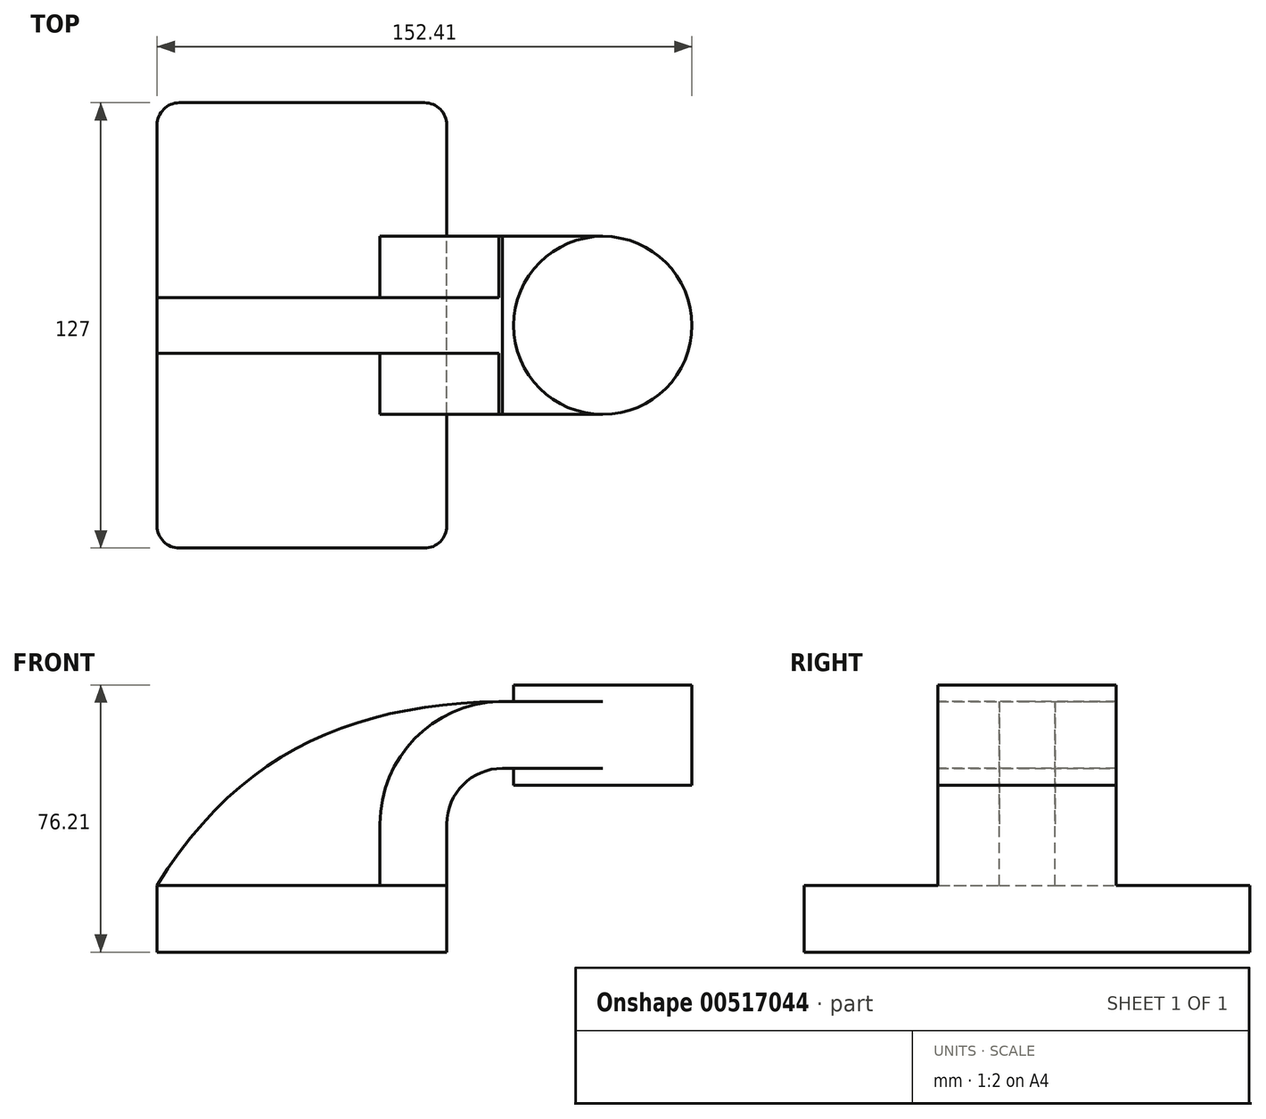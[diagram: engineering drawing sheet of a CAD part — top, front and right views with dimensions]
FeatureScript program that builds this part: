
annotation { "Feature Type Name" : "Feature", "Feature Type Description" : "" }
export const myFeature = defineFeature(function(context is Context, id is Id, definition is map)
    precondition{}
    {
        {
            var Q0;
            Q0=qCreatedBy(makeId("Front.planeOp"),FACE);
            var sketch = newSketch(context, id + "F0", { "sketchPlane" : qUnion([Q0])});
            skLineSegment(sketch, "E0.bottom", {"start": v(-41.28, 9.52) * mm, "end": v(41.27, 9.53) * mm});
            skLineSegment(sketch, "E0.top", {"start": v(-41.28, -9.53) * mm, "end": v(41.28, -9.53) * mm});
            skLineSegment(sketch, "E0.left", {"start": v(-41.28, 9.52) * mm, "end": v(-41.27, -9.53) * mm});
            skLineSegment(sketch, "E0.right", {"start": v(41.28, 9.53) * mm, "end": v(41.28, -9.52) * mm});
            skPoint(sketch, "E0.middle", {"position": v(0, 0) * mm});
            skLineSegment(sketch, "E1.bottom", {"start": v(60.32, 66.68) * mm, "end": v(111.12, 66.68) * mm});
            skLineSegment(sketch, "E1.top", {"start": v(60.32, 38.1) * mm, "end": v(111.12, 38.1) * mm});
            skLineSegment(sketch, "E1.left", {"start": v(60.32, 66.68) * mm, "end": v(60.32, 38.1) * mm});
            skLineSegment(sketch, "E1.right", {"start": v(111.12, 66.68) * mm, "end": v(111.12, 38.1) * mm});
            skPoint(sketch, "E1.middle", {"position": v(85.72, 52.39) * mm});
            skLineSegment(sketch, "E2", {"start": v(41.27, 9.53) * mm, "end": v(41.27, 27) * mm});
            skArc(sketch, "E3", {"start": v(41.27, 27) * mm, "mid": v(45.92, 38.23) * mm, "end": v(57.15, 42.88) * mm});
            skLineSegment(sketch, "E4", {"start": v(57.15, 42.88) * mm, "end": v(85.72, 42.88) * mm});
            skLineSegment(sketch, "E5.0", {"start": v(57.15, 61.93) * mm, "end": v(85.72, 61.93) * mm});
            skArc(sketch, "E5.1", {"start": v(22.23, 27) * mm, "mid": v(32.45, 51.7) * mm, "end": v(57.15, 61.93) * mm});
            skLineSegment(sketch, "E5.2", {"start": v(22.22, 9.53) * mm, "end": v(22.22, 27) * mm});
            skFitSpline(sketch, "E6", {"points": [v(-41.28, 9.53) * mm, v(57.15, 61.93) * mm], "startDerivative": vector(69.81, 113.57) * mm, "endDerivative": vector(128.26, 1.5) * mm});
            skLineSegment(sketch, "E7", {"start": v(85.72, 38.1) * mm, "end": v(85.72, 66.68) * mm});
            skSolve(sketch);
        }
        {
            var Q0;
            Q0=makeQuery(id+"F0.imprint","IMPRINT",FACE,{"disambiguationData":[TD([[makeQuery(id+"F0.imprint","IMPRINT",EDGE,{"derivedFrom":sQuery(id+"F0.wireOp",EDGE,"E0.top")}),1.0]])]});
            extrude(context, id + "F1", {"entities" : qUnion([Q0]), "endBound" : BoundingType.SYMMETRIC, "depth" : 127 * mm});
        }
        {
            var Q0;
            {var subQ1=sQuery(id+"F0.wireOp",EDGE,"E2");Q0=makeQuery(id+"F0.imprint","IMPRINT",FACE,{"disambiguationData":[TD([[makeQuery(id+"F0.imprint","IMPRINT",EDGE,{"derivedFrom":subQ1}),1.0]])]});}
            var Q1;
            {var subQ0=sQuery(id+"F0.wireOp",EDGE,"E5.0");var subQ1=sQuery(id+"F0.wireOp",EDGE,"E1.left");var subQ2=makeQuery(id+"F0.imprint","INTERSECT",VERTEX,{"derivedFrom":[subQ1,subQ0]});Q1=makeQuery(id+"F0.imprint","IMPRINT",FACE,{"disambiguationData":[TD([[makeQuery(id+"F0.imprint","IMPRINT",EDGE,{"disambiguationData":[TD([[subQ2,-1.0]])],"derivedFrom":subQ1}),1.0]])]});}
            extrude(context, id + "F2", {"entities" : qUnion([Q0, Q1]), "operationType" : NewBodyOperationType.ADD, "endBound" : BoundingType.SYMMETRIC, "depth" : 50.8 * mm});
        }
        {
            var Q0;
            {var subQ3=sQuery(id+"F0.wireOp",EDGE,"E5.2");Q0=makeQuery(id+"F0.imprint","IMPRINT",FACE,{"disambiguationData":[TD([[makeQuery(id+"F0.imprint","IMPRINT",EDGE,{"derivedFrom":subQ3}),1.0]])]});}
            extrude(context, id + "F3", {"entities" : qUnion([Q0]), "operationType" : NewBodyOperationType.ADD, "endBound" : BoundingType.SYMMETRIC, "depth" : 15.88 * mm});
        }
        {
            var Q0;
            {var subQ4=sQuery(id+"F0.wireOp",EDGE,"E1.right");Q0=makeQuery(id+"F0.imprint","IMPRINT",FACE,{"disambiguationData":[TD([[makeQuery(id+"F0.imprint","IMPRINT",EDGE,{"derivedFrom":subQ4}),-1.0]])]});}
            var Q1;
            Q1=sQuery(id+"F0.wireOp",EDGE,"E7");
            revolve(context, id + "F4", {"operationType" : NewBodyOperationType.ADD, "entities" : qUnion([Q0]), "axis" : qUnion([Q1]), "revolveType" : RevolveType.FULL});
        }
        {
            var Q0;
            Q0=makeQuery(id+"F1.opExtrude","CAP_EDGE",EDGE,{"disambiguationData":[OSD([sQuery(id+"F0.wireOp",EDGE,"E0.right")])],"isStart":false});
            var Q1;
            Q1=makeQuery(id+"F1.opExtrude","CAP_EDGE",EDGE,{"disambiguationData":[OSD([sQuery(id+"F0.wireOp",EDGE,"E0.left")])],"isStart":false});
            var Q2;
            Q2=makeQuery(id+"F1.opExtrude","CAP_EDGE",EDGE,{"disambiguationData":[OSD([sQuery(id+"F0.wireOp",EDGE,"E0.right")])],"isStart":true});
            var Q3;
            Q3=makeQuery(id+"F1.opExtrude","CAP_EDGE",EDGE,{"disambiguationData":[OSD([sQuery(id+"F0.wireOp",EDGE,"E0.left")])],"isStart":true});
            fillet(context, id + "F5", {"entities" : qUnion([Q0, Q1, Q2, Q3]), "radius" : 6.35 * mm, "tangentPropagation" : true, "allowEdgeOverflow" : false});
        }
    });
